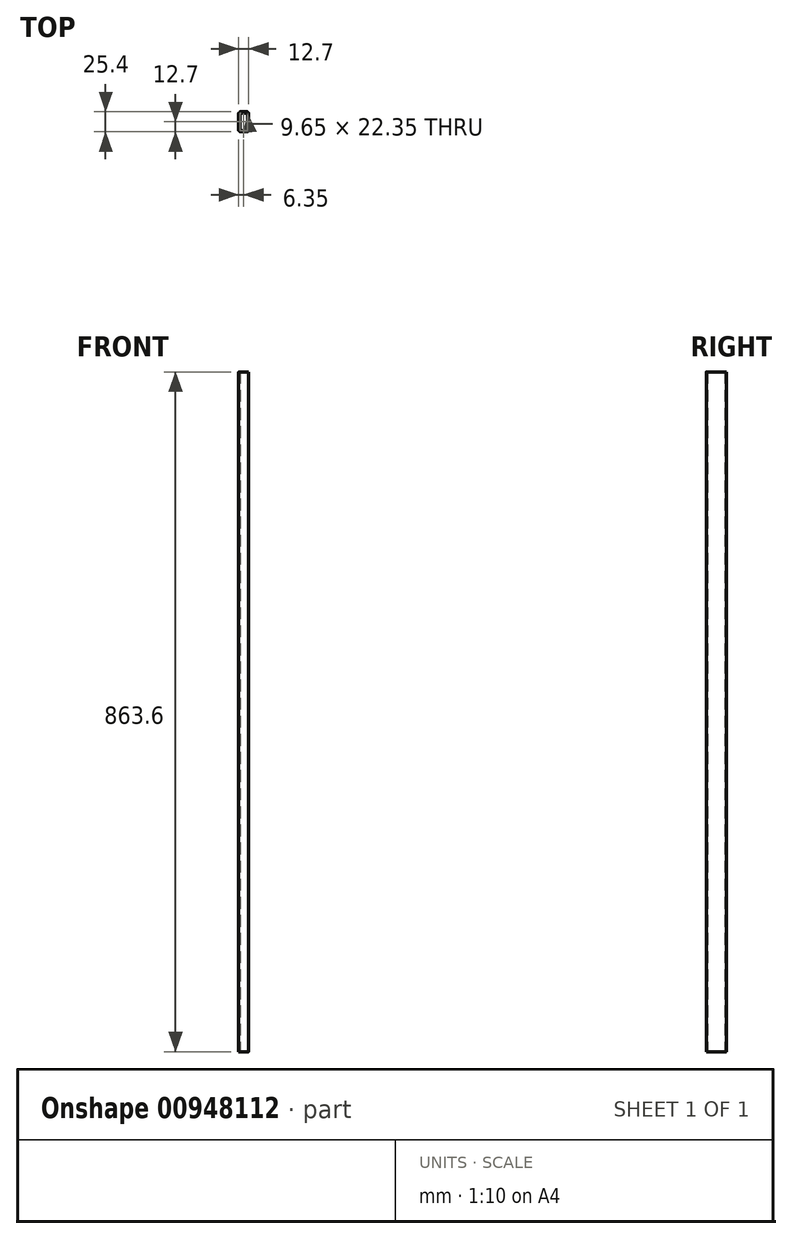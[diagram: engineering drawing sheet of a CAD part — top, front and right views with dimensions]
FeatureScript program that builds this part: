
annotation { "Feature Type Name" : "Feature", "Feature Type Description" : "" }
export const myFeature = defineFeature(function(context is Context, id is Id, definition is map)
    precondition{}
    {
        {
            var Q0;
            Q0=qCreatedBy(makeId("Top.planeOp"),FACE);
            var sketch = newSketch(context, id + "F0", { "sketchPlane" : qUnion([Q0])});
            skLineSegment(sketch, "E0.bottom", {"start": v(6.35, 12.7) * mm, "end": v(-6.35, 12.7) * mm});
            skLineSegment(sketch, "E0.top", {"start": v(6.35, -12.7) * mm, "end": v(-6.35, -12.7) * mm});
            skLineSegment(sketch, "E0.left", {"start": v(6.35, 12.7) * mm, "end": v(6.35, -12.7) * mm});
            skLineSegment(sketch, "E0.right", {"start": v(-6.35, 12.7) * mm, "end": v(-6.35, -12.7) * mm});
            skPoint(sketch, "E0.middle", {"position": v(0, 0) * mm});
            skLineSegment(sketch, "E1.bottom", {"start": v(4.83, 11.18) * mm, "end": v(-4.83, 11.18) * mm});
            skLineSegment(sketch, "E1.top", {"start": v(4.83, -11.18) * mm, "end": v(-4.83, -11.18) * mm});
            skLineSegment(sketch, "E1.left", {"start": v(4.83, 11.18) * mm, "end": v(4.83, -11.18) * mm});
            skLineSegment(sketch, "E1.right", {"start": v(-4.83, 11.18) * mm, "end": v(-4.83, -11.18) * mm});
            skSolve(sketch);
        }
        {
            var Q0;
            Q0=makeQuery(id+"F0.imprint","IMPRINT",FACE,{"disambiguationData":[TD([[makeQuery(id+"F0.imprint","IMPRINT",EDGE,{"derivedFrom":sQuery(id+"F0.wireOp",EDGE,"E0.bottom")}),1.0]])]});
            extrude(context, id + "F1", {"entities" : qUnion([Q0]), "depth" : 863.6 * mm, "offsetDistance" : 25 * mm});
        }
        {
            var Q0;
            Q0=makeQuery(id+"F1.opExtrude","SWEPT_EDGE",EDGE,{"disambiguationData":[OSD([sQuery(id+"F0.wireOp",EDGE,"E0.bottom"),sQuery(id+"F0.wireOp",EDGE,"E0.right")])]});
            var Q1;
            Q1=makeQuery(id+"F1.opExtrude","SWEPT_EDGE",EDGE,{"disambiguationData":[OSD([sQuery(id+"F0.wireOp",EDGE,"E0.bottom"),sQuery(id+"F0.wireOp",EDGE,"E0.left")])]});
            var Q2;
            Q2=makeQuery(id+"F1.opExtrude","SWEPT_EDGE",EDGE,{"disambiguationData":[OSD([sQuery(id+"F0.wireOp",EDGE,"E0.top"),sQuery(id+"F0.wireOp",EDGE,"E0.left")])]});
            var Q3;
            Q3=makeQuery(id+"F1.opExtrude","SWEPT_EDGE",EDGE,{"disambiguationData":[OSD([sQuery(id+"F0.wireOp",EDGE,"E0.top"),sQuery(id+"F0.wireOp",EDGE,"E0.right")])]});
            fillet(context, id + "F2", {"entities" : qUnion([Q0, Q1, Q2, Q3]), "radius" : 2.5 * mm, "tangentPropagation" : true, "allowEdgeOverflow" : false});
        }
    });
